# Revit family: Domotics-NetworkCabling-GEWISS-CABINETS_FLOOR-MOUNTED_19_30U_D600
name_source: partatom
category: Apparecchi elettrici
units: mm (PartAtom-declared; Revit-internal decimal feet)

## family parameters
Condiviso = No
Host = Superficie
Mantenere orientamento annotazione = Sì
Numero OmniClass = 23.80.30.00
Punto di calcolo locali = Sì
Quota connettore circolare = Usa diametro
Taglio con vuoti quando caricato = No
Tipo di parte = Normale
Titolo OmniClass = Distribution Devices

## types (1)
- GW38452 - FLOOR RACK CABINET 19 30U 600x600MM
    Cabling unity = 30 U
    Catalogue = DOMOTICS
    Category = 19â€ floor-standing cabinet
    Colour = Grey (RAL 7035)
    Depth (mm) = 600 mm
    Descrizione = FLOOR RACK CABINET 19 30U 600x600MM
    Door opening = 135°
    Electrocod = 3752
    Finishing = Textured
    IDF = c02ffb6e-b0a0-4f89-afd4-66ad6daed70d
    IDT = 39e0a6a38c734b9c98aba4b4c497b8be
    IP degree = IP20
    Immagine tipo = C.jpg
    Material = Steel
    Modello = GW38452
    No. uprights = 2
    Outer dim. LxHxD (mm) = 600x1485x600
    Produttore = GEWISS S.p.A.
    Prospetto di default = 900 mm  [stored 2.95276 ft]
    SEO = Cabinet
    Static load capacity = 1000KG
    Technical sheet = https://www.gewiss.com
    Type of door = Reversible
    URL = https://www.gewiss.com
    Version file RFA = 21.2
    barra din = Sì
    n_poli = 1

note: [stored X ft] marks values corroborated as IEEE doubles in the binary element streams (Revit-internal decimal feet)

## geometry (parser evidence)
native form markers: Sweep x3
no freeform markers — native parametric forms only
